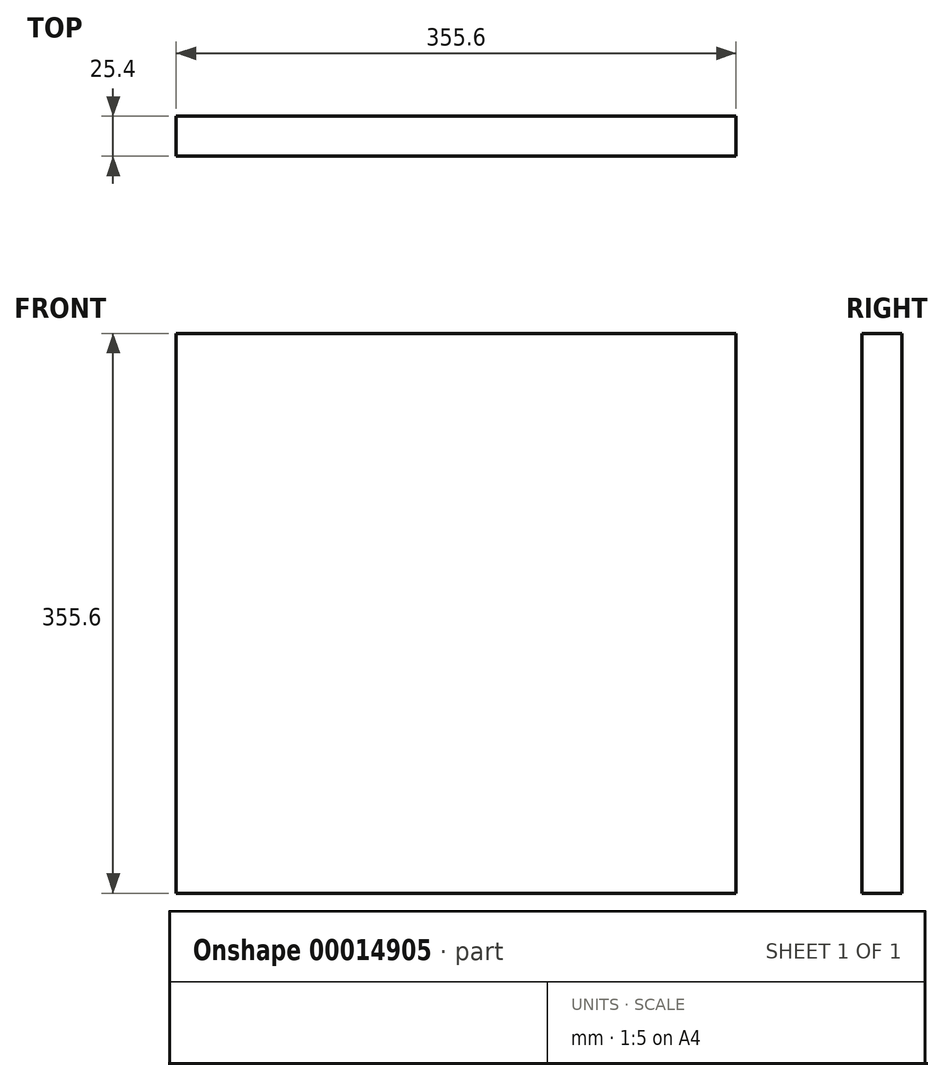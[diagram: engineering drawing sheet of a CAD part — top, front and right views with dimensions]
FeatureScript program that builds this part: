
annotation { "Feature Type Name" : "Feature", "Feature Type Description" : "" }
export const myFeature = defineFeature(function(context is Context, id is Id, definition is map)
    precondition{}
    {
        {
            var Q0;
            Q0=qCreatedBy(makeId("Front.planeOp"),FACE);
            var sketch = newSketch(context, id + "F0", { "sketchPlane" : qUnion([Q0])});
            skLineSegment(sketch, "E0.bottom", {"start": v(0, 0) * mm, "end": v(-355.6, 0) * mm});
            skLineSegment(sketch, "E0.top", {"start": v(0, 355.6) * mm, "end": v(-355.6, 355.6) * mm});
            skLineSegment(sketch, "E0.left", {"start": v(0, 0) * mm, "end": v(0, 355.6) * mm});
            skLineSegment(sketch, "E0.right", {"start": v(-355.6, 0) * mm, "end": v(-355.6, 355.6) * mm});
            skSolve(sketch);
        }
        {
            var Q0;
            Q0 = qSketchRegion(id + "F0", true);
            extrude(context, id + "F1", {"entities" : qUnion([Q0]), "depth" : 25.4 * mm});
        }
    });
